# Revit family: EM 30 2P
name_source: partatom
category: Specialty Equipment
revit_build: Autodesk Revit 2017 (Build: 20160225_1515(x64)
units: mm (PartAtom-declared; Revit-internal decimal feet)

## family parameters
Cut with Voids When Loaded = Yes
Host = Face
Part Type = Normal
Room Calculation Point = No
Round Connector Dimension = Use Diameter
Shared = No

## types (1)
- EM 30 2P
    Alto encastre = -80 mm  [stored -0.262467 ft]
    Ancho Encastre = 280 mm  [stored 0.918635 ft]
    Ca_1_Cable de conexión = 900 mm  [stored 2.95276 ft]
    Ca_1_Frecuencia Hz. = 50
    Ca_1_Potencia nominal max. W. = 3000
    Ca_2_Placa Eléctrica Ø 145 / 1.000 W. = -
    Ca_2_Placa Eléctrica Ø 145 / 1.500 W. = 1
    Ca_2_Placa Eléctrica Ø 180 / 1.500 W. = 1
    Ca_2_Placa Eléctrica Ø 180 / 2.000 W. = -
    Ca_2_Quemador auxiliar - 1,00 Kw. = -
    Ca_2_Quemador rápido - 2,80 Kw. = -
    Ca_2_Quemador rápido - 3,00 Kw. = -
    Ca_2_Quemador semi-rápido - 1,75 Kw. = -
    Ca_2_Quemador tipo pecera - 2,8 Kw. = -
    Ca_2_Quemador triple anillo - 3,10 Kw = -
    Ca_3_Encendido electrónico = Yes
    Ca_3_Mandos incorporados = Yes
    Ca_3_Piloto indicativo de funcionamiento = Yes
    Ca_4_Parrilla para cocinar sobre los quemadores = No
    Ca_4_Parrillas de fundición para cocinar sobre los quemadores = No
    Ca_4_Parrillas individuales = No
    Ca_4_Suplemento recipiente pequeño = No
    Ca_5_Seguridad por termopar = No
    Ca_6_Color Blanco = No
    Ca_6_Color Inox = Yes
    Ca_6_Encimera rectangular = Yes
    Ca_6_Marco inox = No
    Ca_Alto = 40 mm  [stored 0.131234 ft]
    Ca_Ancho = 300 mm
    Ca_Ancho Interior = 280 mm  [stored 0.918635 ft]
    Ca_Certificación (Chile) = E-013-01- 24227
    Ca_Creado por = Catálogo Arquitectura
    Ca_Código Catálogo Arquitectura = 465_TEK_035
    Ca_Código EAN = 8421152033258
    Ca_Código del Producto = 10209011
    Ca_Especificaciones Técnicas = Placa de cocción eléctrica empotrable para cocina modelo EM 30 2P
    Ca_Fabricante = Teka
    Ca_Instalación = Empotrable
    Ca_Itemizado CDT = E 08 06 02
    Ca_Masterformat = 11 30 13.13
    Ca_Material Principal = Acero inoxidable austenítico
    Ca_Medidas de embalaje = 36 x 58 x 12
    Ca_País de Fabricación = Turquía
    Ca_Peso = 5,5 kg
    Ca_Producto = Placa de cocción eléctrica IR 9547
    Ca_Profundidad = 510 mm  [stored 1.67323 ft]
    Ca_Profundidad Interior = 490 mm  [stored 1.60761 ft]
    Ca_Representante = Teka
    Ca_Teléfono = 99821 1017
    Ca_Usos = Placa de cocción eléctrica empotrable para mueble de cocina
    Ca_Web del Fabricante = www.teka.cl
    Ca_Web del Representante = www.teka.cl
    Cubierta encimera = Teka_Acero inoxidable austenítico
    Default Elevation = 1219.2 mm  [stored 4 ft]
    Description = Placa de cocción eléctrica empotrable para mueble de cocina
    Disco Inducción = Teka_Interior Negro
    Interior encimera = Teka_Aluminio
    Luz encendido = Teka_Menu Luz Roja
    Manufacturer = Teka
    Model = EM 30 2P
    Profundidad encastre = 490 mm  [stored 1.60761 ft]
    URL = www.teka.cl
    Voltage = 220V
    Wattage = 3000

note: [stored X ft] marks values corroborated as IEEE doubles in the binary element streams (Revit-internal decimal feet)

## geometry (parser evidence)
native form markers: Sweep x9
no freeform markers — native parametric forms only
